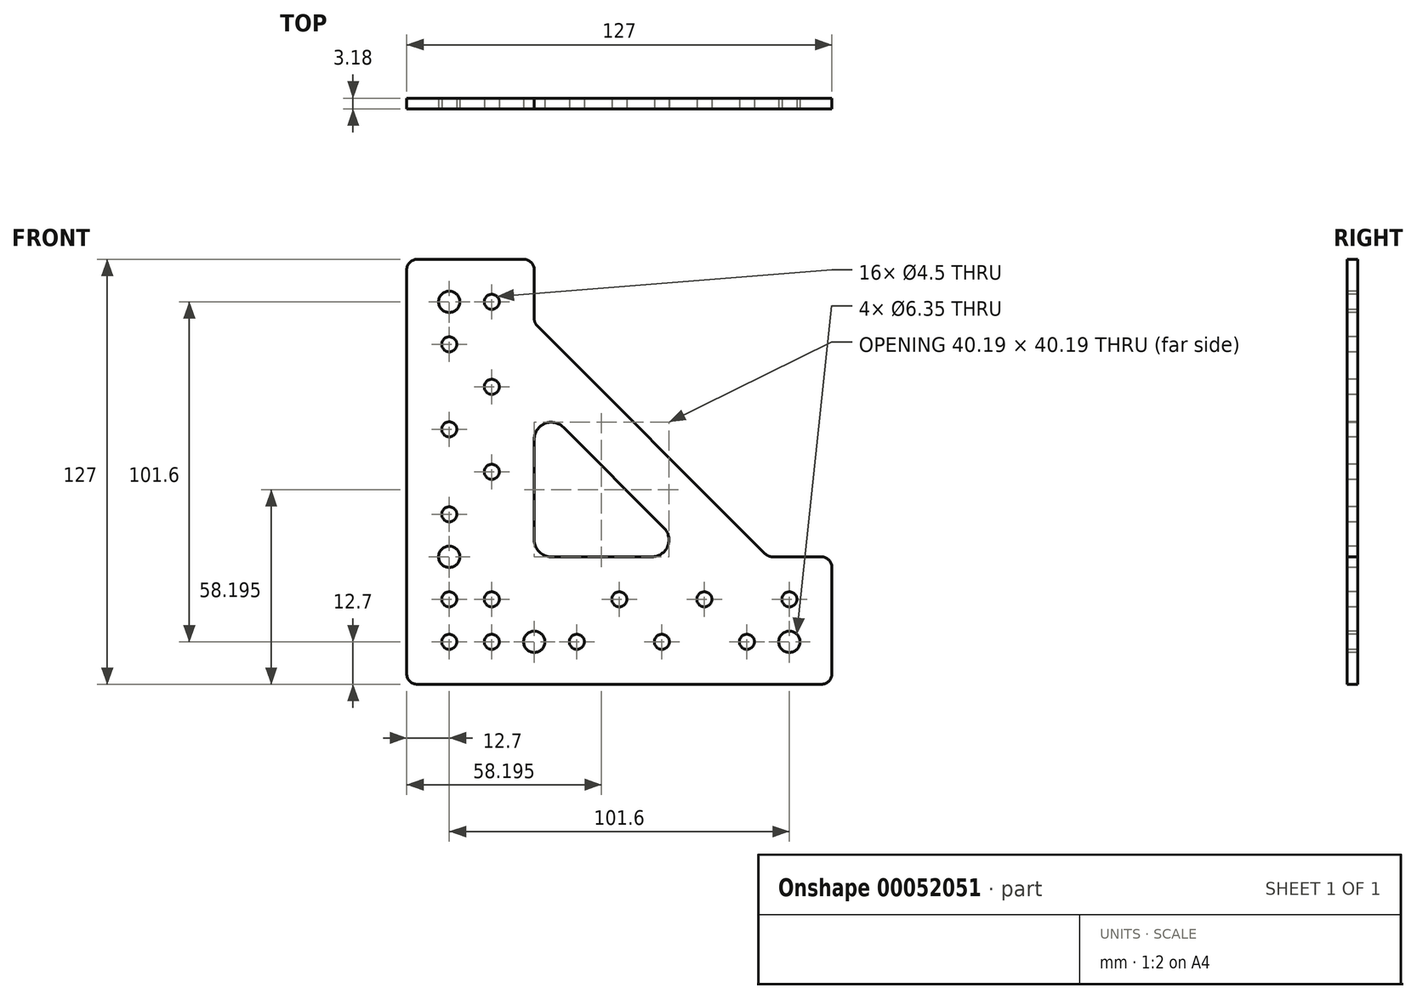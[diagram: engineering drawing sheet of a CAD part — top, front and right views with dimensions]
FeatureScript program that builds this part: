
annotation { "Feature Type Name" : "Feature", "Feature Type Description" : "" }
export const myFeature = defineFeature(function(context is Context, id is Id, definition is map)
    precondition{}
    {
        {
            var Q0;
            Q0=qCreatedBy(makeId("Front.planeOp"),FACE);
            var sketch = newSketch(context, id + "F0", { "sketchPlane" : qUnion([Q0])});
            skLineSegment(sketch, "E0.rect.bottom", {"start": v(-63.5, 63.5) * mm, "end": v(-25.4, 63.5) * mm});
            skLineSegment(sketch, "E0.rect.top", {"start": v(-63.5, -63.5) * mm, "end": v(63.5, -63.5) * mm});
            skLineSegment(sketch, "E0.rect.left", {"start": v(-63.5, 63.5) * mm, "end": v(-63.5, -63.5) * mm});
            skLineSegment(sketch, "E0.rect.right", {"start": v(63.5, -25.4) * mm, "end": v(63.5, -63.5) * mm});
            skPoint(sketch, "E0.rect.middle", {"position": v(0, 0) * mm});
            skLineSegment(sketch, "E1", {"start": v(-25.4, 63.5) * mm, "end": v(-25.4, 44.45) * mm});
            skLineSegment(sketch, "E2", {"start": v(63.5, -25.4) * mm, "end": v(44.45, -25.4) * mm});
            skLineSegment(sketch, "E3", {"start": v(-25.4, 44.45) * mm, "end": v(44.45, -25.4) * mm});
            skLineSegment(sketch, "E4", {"start": v(-25.4, 22) * mm, "end": v(22, -25.4) * mm});
            skPoint(sketch, "E5.orphan", {"position": v(63.5, 63.5) * mm});
            skLineSegment(sketch, "E6.trimOffspring", {"start": v(-25.4, 22) * mm, "end": v(-25.4, -25.4) * mm});
            skLineSegment(sketch, "E7.trimOffspring", {"start": v(22, -25.4) * mm, "end": v(-25.4, -25.4) * mm});
            skSolve(sketch);
        }
        {
            var Q0;
            Q0=makeQuery(id+"F0.imprint","IMPRINT",FACE,{"disambiguationData":[TD([[makeQuery(id+"F0.imprint","IMPRINT",EDGE,{"derivedFrom":sQuery(id+"F0.wireOp",EDGE,"E0.rect.bottom")}),-1.0]])]});
            extrude(context, id + "F1", {"entities" : qUnion([Q0]), "depth" : 3.17 * mm});
        }
        {
            var Q0;
            Q0=makeQuery(id+"F1.opExtrude","SWEPT_EDGE",EDGE,{"disambiguationData":[OSD([sQuery(id+"F0.wireOp",EDGE,"E0.rect.bottom"),sQuery(id+"F0.wireOp",EDGE,"E1")])]});
            var Q1;
            Q1=makeQuery(id+"F1.opExtrude","SWEPT_EDGE",EDGE,{"disambiguationData":[OSD([sQuery(id+"F0.wireOp",EDGE,"E1"),sQuery(id+"F0.wireOp",EDGE,"E3")])]});
            var Q2;
            Q2=makeQuery(id+"F1.opExtrude","SWEPT_EDGE",EDGE,{"disambiguationData":[OSD([sQuery(id+"F0.wireOp",EDGE,"E2"),sQuery(id+"F0.wireOp",EDGE,"E3")])]});
            var Q3;
            Q3=makeQuery(id+"F1.opExtrude","SWEPT_EDGE",EDGE,{"disambiguationData":[OSD([sQuery(id+"F0.wireOp",EDGE,"E0.rect.right"),sQuery(id+"F0.wireOp",EDGE,"E2")])]});
            var Q4;
            Q4=makeQuery(id+"F1.opExtrude","SWEPT_EDGE",EDGE,{"disambiguationData":[OSD([sQuery(id+"F0.wireOp",EDGE,"E0.rect.top"),sQuery(id+"F0.wireOp",EDGE,"E0.rect.right")])]});
            var Q5;
            Q5=makeQuery(id+"F1.opExtrude","SWEPT_EDGE",EDGE,{"disambiguationData":[OSD([sQuery(id+"F0.wireOp",EDGE,"E0.rect.top"),sQuery(id+"F0.wireOp",EDGE,"E0.rect.left")])]});
            var Q6;
            Q6=makeQuery(id+"F1.opExtrude","SWEPT_EDGE",EDGE,{"disambiguationData":[OSD([sQuery(id+"F0.wireOp",EDGE,"E0.rect.bottom"),sQuery(id+"F0.wireOp",EDGE,"E0.rect.left")])]});
            fillet(context, id + "F2", {"entities" : qUnion([Q0, Q1, Q2, Q3, Q4, Q5, Q6]), "radius" : 3.17 * mm, "tangentPropagation" : true, "allowEdgeOverflow" : false});
        }
        {
            var Q0;
            Q0=makeQuery(id+"F1.opExtrude","SWEPT_EDGE",EDGE,{"disambiguationData":[OSD([sQuery(id+"F0.wireOp",EDGE,"E4"),sQuery(id+"F0.wireOp",EDGE,"E7.trimOffspring")])]});
            var Q1;
            Q1=makeQuery(id+"F1.opExtrude","SWEPT_EDGE",EDGE,{"disambiguationData":[OSD([sQuery(id+"F0.wireOp",EDGE,"E6.trimOffspring"),sQuery(id+"F0.wireOp",EDGE,"E7.trimOffspring")])]});
            var Q2;
            Q2=makeQuery(id+"F1.opExtrude","SWEPT_EDGE",EDGE,{"disambiguationData":[OSD([sQuery(id+"F0.wireOp",EDGE,"E4"),sQuery(id+"F0.wireOp",EDGE,"E6.trimOffspring")])]});
            fillet(context, id + "F3", {"entities" : qUnion([Q0, Q1, Q2]), "radius" : 5.08 * mm, "tangentPropagation" : true, "allowEdgeOverflow" : false});
        }
        {
            var Q0;
            Q0=makeQuery(id+"F1.opExtrude","CAP_FACE",FACE,{"disambiguationData":[OSD([sQuery(id+"F0.wireOp",EDGE,"E0.rect.bottom"),sQuery(id+"F0.wireOp",EDGE,"E0.rect.top"),sQuery(id+"F0.wireOp",EDGE,"E0.rect.left"),sQuery(id+"F0.wireOp",EDGE,"E0.rect.right"),sQuery(id+"F0.wireOp",EDGE,"E1"),sQuery(id+"F0.wireOp",EDGE,"E2"),sQuery(id+"F0.wireOp",EDGE,"E3"),sQuery(id+"F0.wireOp",EDGE,"E4"),sQuery(id+"F0.wireOp",EDGE,"E6.trimOffspring"),sQuery(id+"F0.wireOp",EDGE,"E7.trimOffspring")])],"isStart":false});
            var sketch = newSketch(context, id + "F4", { "sketchPlane" : qUnion([Q0])});
            skLineSegment(sketch, "E8", {"start": v(-50.8, 66.32) * mm, "end": v(-50.8, -65.15) * mm, "construction": true});
            skLineSegment(sketch, "E9", {"start": v(65.1, -50.8) * mm, "end": v(-84.42, -50.8) * mm, "construction": true});
            skLineSegment(sketch, "E10", {"start": v(-38.1, 66.32) * mm, "end": v(-38.1, -66.32) * mm, "construction": true});
            skLineSegment(sketch, "E11", {"start": v(73.12, -38.1) * mm, "end": v(-89.34, -38.1) * mm, "construction": true});
            skPoint(sketch, "E12", {"position": v(-50.8, -50.8) * mm});
            skPoint(sketch, "E13", {"position": v(-50.8, -38.1) * mm});
            skPoint(sketch, "E14", {"position": v(-38.1, -38.1) * mm});
            skPoint(sketch, "E15", {"position": v(-38.1, -50.8) * mm});
            skPoint(sketch, "E16", {"position": v(-50.8, 50.8) * mm});
            skPoint(sketch, "E17", {"position": v(-38.1, 50.8) * mm});
            skPoint(sketch, "E18", {"position": v(-50.8, 38.1) * mm});
            skPoint(sketch, "E19", {"position": v(-38.1, 25.4) * mm});
            skPoint(sketch, "E20", {"position": v(-50.8, 12.7) * mm});
            skPoint(sketch, "E21", {"position": v(-38.1, 0) * mm});
            skPoint(sketch, "E22", {"position": v(-50.8, -12.7) * mm});
            skPoint(sketch, "E23", {"position": v(-50.8, -25.4) * mm});
            skPoint(sketch, "E24", {"position": v(50.8, -50.8) * mm});
            skPoint(sketch, "E25", {"position": v(50.8, -38.1) * mm});
            skPoint(sketch, "E26", {"position": v(38.1, -50.8) * mm});
            skPoint(sketch, "E27", {"position": v(12.7, -50.8) * mm});
            skPoint(sketch, "E28", {"position": v(-12.7, -50.8) * mm});
            skPoint(sketch, "E29", {"position": v(-25.4, -50.8) * mm});
            skPoint(sketch, "E30", {"position": v(25.4, -38.1) * mm});
            skPoint(sketch, "E31", {"position": v(0, -38.1) * mm});
            skSolve(sketch);
        }
        {
            var Q0;
            Q0=sQuery(id+"F4.wireOp",VERTEX,"E16");
            var Q1;
            Q1=sQuery(id+"F4.wireOp",VERTEX,"E23");
            var Q2;
            Q2=sQuery(id+"F4.wireOp",VERTEX,"E24");
            var Q3;
            Q3=sQuery(id+"F4.wireOp",VERTEX,"E29");
            var Q4;
            Q4=makeQuery(id+"F1.opExtrude","SWEPT_BODY",BODY,{"disambiguationData":[OSD([sQuery(id+"F0.wireOp",EDGE,"E0.rect.bottom"),sQuery(id+"F0.wireOp",EDGE,"E0.rect.top"),sQuery(id+"F0.wireOp",EDGE,"E0.rect.left"),sQuery(id+"F0.wireOp",EDGE,"E0.rect.right"),sQuery(id+"F0.wireOp",EDGE,"E1"),sQuery(id+"F0.wireOp",EDGE,"E2"),sQuery(id+"F0.wireOp",EDGE,"E3"),sQuery(id+"F0.wireOp",EDGE,"E4"),sQuery(id+"F0.wireOp",EDGE,"E6.trimOffspring"),sQuery(id+"F0.wireOp",EDGE,"E7.trimOffspring")])]});
            hole(context, id + "F5", {"style" : HoleStyle.SIMPLE, "holeDiameter" : 6.35 * mm, "endStyle" : HoleEndStyle.THROUGH, "locations" : qUnion([Q0, Q1, Q2, Q3]), "scope" : qUnion([Q4])});
        }
        {
            var Q0;
            Q0=sQuery(id+"F4.wireOp",VERTEX,"E18");
            var Q1;
            Q1=sQuery(id+"F4.wireOp",VERTEX,"E17");
            var Q2;
            Q2=sQuery(id+"F4.wireOp",VERTEX,"E19");
            var Q3;
            Q3=sQuery(id+"F4.wireOp",VERTEX,"E20");
            var Q4;
            Q4=sQuery(id+"F4.wireOp",VERTEX,"E21");
            var Q5;
            Q5=sQuery(id+"F4.wireOp",VERTEX,"E22");
            var Q6;
            Q6=sQuery(id+"F4.wireOp",VERTEX,"E14");
            var Q7;
            Q7=sQuery(id+"F4.wireOp",VERTEX,"E13");
            var Q8;
            Q8=sQuery(id+"F4.wireOp",VERTEX,"E12");
            var Q9;
            Q9=sQuery(id+"F4.wireOp",VERTEX,"E15");
            var Q10;
            Q10=sQuery(id+"F4.wireOp",VERTEX,"E28");
            var Q11;
            Q11=sQuery(id+"F4.wireOp",VERTEX,"E31");
            var Q12;
            Q12=sQuery(id+"F4.wireOp",VERTEX,"E27");
            var Q13;
            Q13=sQuery(id+"F4.wireOp",VERTEX,"E30");
            var Q14;
            Q14=sQuery(id+"F4.wireOp",VERTEX,"E26");
            var Q15;
            Q15=sQuery(id+"F4.wireOp",VERTEX,"E25");
            var Q16;
            Q16=makeQuery(id+"F1.opExtrude","SWEPT_BODY",BODY,{"disambiguationData":[OSD([sQuery(id+"F0.wireOp",EDGE,"E0.rect.bottom"),sQuery(id+"F0.wireOp",EDGE,"E0.rect.top"),sQuery(id+"F0.wireOp",EDGE,"E0.rect.left"),sQuery(id+"F0.wireOp",EDGE,"E0.rect.right"),sQuery(id+"F0.wireOp",EDGE,"E1"),sQuery(id+"F0.wireOp",EDGE,"E2"),sQuery(id+"F0.wireOp",EDGE,"E3"),sQuery(id+"F0.wireOp",EDGE,"E4"),sQuery(id+"F0.wireOp",EDGE,"E6.trimOffspring"),sQuery(id+"F0.wireOp",EDGE,"E7.trimOffspring")])]});
            hole(context, id + "F6", {"style" : HoleStyle.SIMPLE, "holeDiameter" : 4.5 * mm, "endStyle" : HoleEndStyle.THROUGH, "locations" : qUnion([Q0, Q1, Q2, Q3, Q4, Q5, Q6, Q7, Q8, Q9, Q10, Q11, Q12, Q13, Q14, Q15]), "scope" : qUnion([Q16])});
        }
    });
